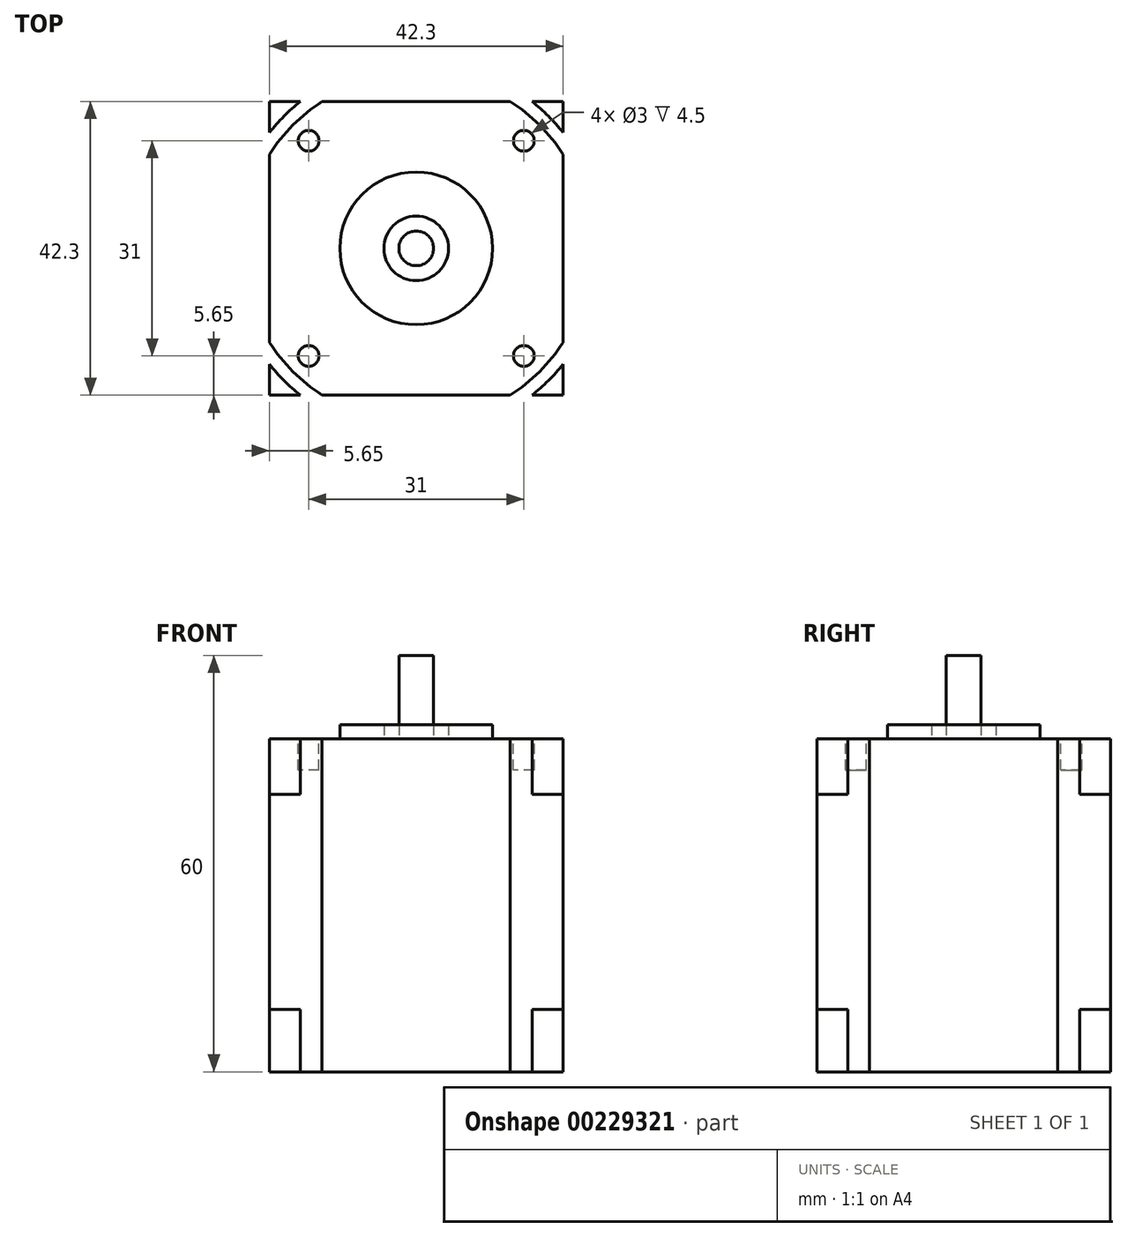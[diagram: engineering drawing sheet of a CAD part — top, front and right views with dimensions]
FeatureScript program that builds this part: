
annotation { "Feature Type Name" : "Feature", "Feature Type Description" : "" }
export const myFeature = defineFeature(function(context is Context, id is Id, definition is map)
    precondition{}
    {
        {
            var Q0;
            Q0=qCreatedBy(makeId("Top.planeOp"),FACE);
            var sketch = newSketch(context, id + "F0", { "sketchPlane" : qUnion([Q0])});
            skLineSegment(sketch, "E0.bottom", {"start": v(21.15, -21.15) * mm, "end": v(-21.15, -21.15) * mm});
            skLineSegment(sketch, "E0.top", {"start": v(21.15, 21.15) * mm, "end": v(-21.15, 21.15) * mm});
            skLineSegment(sketch, "E0.left", {"start": v(21.15, -21.15) * mm, "end": v(21.15, 21.15) * mm});
            skLineSegment(sketch, "E0.right", {"start": v(-21.15, -21.15) * mm, "end": v(-21.15, 21.15) * mm});
            skPoint(sketch, "E0.middle", {"position": v(0, 0) * mm});
            skCircle(sketch, "E1", {"center": v(0, 0) * mm, "radius": 26.94 * mm});
            skCircle(sketch, "E2", {"center": v(0, 0) * mm, "radius": 25.12 * mm});
            skCircle(sketch, "E3", {"center": v(0, 0) * mm, "radius": 4.65 * mm});
            skCircle(sketch, "E4", {"center": v(0, 0) * mm, "radius": 11 * mm});
            skCircle(sketch, "E5", {"center": v(0, 0) * mm, "radius": 2.5 * mm});
            skCircle(sketch, "E6", {"center": v(-15.5, 15.5) * mm, "radius": 1.5 * mm});
            skCircle(sketch, "E7.1.0", {"center": v(-15.5, -15.5) * mm, "radius": 1.5 * mm});
            skCircle(sketch, "E7.2.0", {"center": v(15.5, -15.5) * mm, "radius": 1.5 * mm});
            skCircle(sketch, "E7.3.0", {"center": v(15.5, 15.5) * mm, "radius": 1.5 * mm});
            skSolve(sketch);
        }
        {
            var Q0;
            Q0=makeQuery(id+"F0.imprint","IMPRINT",FACE,{"disambiguationData":[TD([[makeQuery(id+"F0.imprint","IMPRINT",EDGE,{"derivedFrom":sQuery(id+"F0.wireOp",EDGE,"E4")}),-1.0]])]});
            var Q1;
            Q1=makeQuery(id+"F0.imprint","IMPRINT",FACE,{"disambiguationData":[TD([[makeQuery(id+"F0.imprint","IMPRINT",EDGE,{"derivedFrom":sQuery(id+"F0.wireOp",EDGE,"E3")}),-1.0]])]});
            var Q2;
            Q2=makeQuery(id+"F0.imprint","IMPRINT",FACE,{"disambiguationData":[TD([[makeQuery(id+"F0.imprint","IMPRINT",EDGE,{"derivedFrom":sQuery(id+"F0.wireOp",EDGE,"E6")}),1.0]])]});
            var Q3;
            Q3=makeQuery(id+"F0.imprint","IMPRINT",FACE,{"disambiguationData":[TD([[makeQuery(id+"F0.imprint","IMPRINT",EDGE,{"derivedFrom":sQuery(id+"F0.wireOp",EDGE,"E7.3.0")}),1.0]])]});
            var Q4;
            Q4=makeQuery(id+"F0.imprint","IMPRINT",FACE,{"disambiguationData":[TD([[makeQuery(id+"F0.imprint","IMPRINT",EDGE,{"derivedFrom":sQuery(id+"F0.wireOp",EDGE,"E7.2.0")}),1.0]])]});
            var Q5;
            Q5=makeQuery(id+"F0.imprint","IMPRINT",FACE,{"disambiguationData":[TD([[makeQuery(id+"F0.imprint","IMPRINT",EDGE,{"derivedFrom":sQuery(id+"F0.wireOp",EDGE,"E7.1.0")}),1.0]])]});
            var Q6;
            Q6=makeQuery(id+"F0.imprint","IMPRINT",FACE,{"disambiguationData":[TD([[makeQuery(id+"F0.imprint","IMPRINT",EDGE,{"derivedFrom":sQuery(id+"F0.wireOp",EDGE,"E3")}),1.0]])]});
            var Q7;
            Q7=makeQuery(id+"F0.imprint","IMPRINT",FACE,{"disambiguationData":[TD([[makeQuery(id+"F0.imprint","IMPRINT",EDGE,{"derivedFrom":sQuery(id+"F0.wireOp",EDGE,"E5")}),1.0]])]});
            var Q8;
            {var subQ0=sQuery(id+"F0.wireOp",EDGE,"E1");var subQ1=sQuery(id+"F0.wireOp",EDGE,"E0.top");var subQ2=makeQuery(id+"F0.imprint","INTERSECT",VERTEX,{"disambiguationData":[OD(0.0)],"derivedFrom":[subQ1,subQ0]});Q8=makeQuery(id+"F0.imprint","IMPRINT",FACE,{"disambiguationData":[TD([[makeQuery(id+"F0.imprint","IMPRINT",EDGE,{"disambiguationData":[TD([[subQ2,-1.0]])],"derivedFrom":subQ1}),1.0]])]});}
            var Q9;
            {var subQ0=sQuery(id+"F0.wireOp",EDGE,"E1");var subQ1=sQuery(id+"F0.wireOp",EDGE,"E0.top");var subQ2=makeQuery(id+"F0.imprint","INTERSECT",VERTEX,{"disambiguationData":[OD(1.0)],"derivedFrom":[subQ1,subQ0]});Q9=makeQuery(id+"F0.imprint","IMPRINT",FACE,{"disambiguationData":[TD([[makeQuery(id+"F0.imprint","IMPRINT",EDGE,{"disambiguationData":[TD([[subQ2,1.0]])],"derivedFrom":subQ1}),1.0]])]});}
            var Q10;
            {var subQ0=sQuery(id+"F0.wireOp",EDGE,"E1");var subQ1=sQuery(id+"F0.wireOp",EDGE,"E0.bottom");var subQ2=makeQuery(id+"F0.imprint","INTERSECT",VERTEX,{"disambiguationData":[OD(1.0)],"derivedFrom":[subQ1,subQ0]});Q10=makeQuery(id+"F0.imprint","IMPRINT",FACE,{"disambiguationData":[TD([[makeQuery(id+"F0.imprint","IMPRINT",EDGE,{"disambiguationData":[TD([[subQ2,1.0]])],"derivedFrom":subQ1}),-1.0]])]});}
            var Q11;
            {var subQ0=sQuery(id+"F0.wireOp",EDGE,"E1");var subQ1=sQuery(id+"F0.wireOp",EDGE,"E0.bottom");var subQ2=makeQuery(id+"F0.imprint","INTERSECT",VERTEX,{"disambiguationData":[OD(0.0)],"derivedFrom":[subQ1,subQ0]});Q11=makeQuery(id+"F0.imprint","IMPRINT",FACE,{"disambiguationData":[TD([[makeQuery(id+"F0.imprint","IMPRINT",EDGE,{"disambiguationData":[TD([[subQ2,-1.0]])],"derivedFrom":subQ1}),-1.0]])]});}
            extrude(context, id + "F1", {"entities" : qUnion([Q0, Q1, Q2, Q3, Q4, Q5, Q6, Q7, Q8, Q9, Q10, Q11]), "oppositeDirection" : true, "depth" : 48 * mm});
        }
        {
            var Q0;
            {var subQ0=sQuery(id+"F0.wireOp",EDGE,"E1");var subQ1=sQuery(id+"F0.wireOp",EDGE,"E0.top");var subQ2=makeQuery(id+"F0.imprint","INTERSECT",VERTEX,{"disambiguationData":[OD(1.0)],"derivedFrom":[subQ1,subQ0]});Q0=makeQuery(id+"F0.imprint","IMPRINT",FACE,{"disambiguationData":[TD([[makeQuery(id+"F0.imprint","IMPRINT",EDGE,{"disambiguationData":[TD([[subQ2,1.0]])],"derivedFrom":subQ1}),1.0]])]});}
            var Q1;
            {var subQ0=sQuery(id+"F0.wireOp",EDGE,"E1");var subQ1=sQuery(id+"F0.wireOp",EDGE,"E0.bottom");var subQ2=makeQuery(id+"F0.imprint","INTERSECT",VERTEX,{"disambiguationData":[OD(1.0)],"derivedFrom":[subQ1,subQ0]});Q1=makeQuery(id+"F0.imprint","IMPRINT",FACE,{"disambiguationData":[TD([[makeQuery(id+"F0.imprint","IMPRINT",EDGE,{"disambiguationData":[TD([[subQ2,1.0]])],"derivedFrom":subQ1}),-1.0]])]});}
            var Q2;
            {var subQ0=sQuery(id+"F0.wireOp",EDGE,"E1");var subQ1=sQuery(id+"F0.wireOp",EDGE,"E0.top");var subQ2=makeQuery(id+"F0.imprint","INTERSECT",VERTEX,{"disambiguationData":[OD(0.0)],"derivedFrom":[subQ1,subQ0]});Q2=makeQuery(id+"F0.imprint","IMPRINT",FACE,{"disambiguationData":[TD([[makeQuery(id+"F0.imprint","IMPRINT",EDGE,{"disambiguationData":[TD([[subQ2,-1.0]])],"derivedFrom":subQ1}),1.0]])]});}
            var Q3;
            {var subQ0=sQuery(id+"F0.wireOp",EDGE,"E1");var subQ1=sQuery(id+"F0.wireOp",EDGE,"E0.bottom");var subQ2=makeQuery(id+"F0.imprint","INTERSECT",VERTEX,{"disambiguationData":[OD(0.0)],"derivedFrom":[subQ1,subQ0]});Q3=makeQuery(id+"F0.imprint","IMPRINT",FACE,{"disambiguationData":[TD([[makeQuery(id+"F0.imprint","IMPRINT",EDGE,{"disambiguationData":[TD([[subQ2,-1.0]])],"derivedFrom":subQ1}),-1.0]])]});}
            extrude(context, id + "F2", {"entities" : qUnion([Q0, Q1, Q2, Q3]), "operationType" : NewBodyOperationType.REMOVE, "oppositeDirection" : true, "depth" : 39 * mm, "hasSecondDirection" : true, "secondDirectionOppositeDirection" : true, "secondDirectionDepth" : 8 * mm});
        }
        {
            var Q0;
            Q0=makeQuery(id+"F0.imprint","IMPRINT",FACE,{"disambiguationData":[TD([[makeQuery(id+"F0.imprint","IMPRINT",EDGE,{"derivedFrom":sQuery(id+"F0.wireOp",EDGE,"E3")}),-1.0]])]});
            extrude(context, id + "F3", {"entities" : qUnion([Q0]), "operationType" : NewBodyOperationType.ADD, "depth" : 2 * mm});
        }
        {
            var Q0;
            Q0=makeQuery(id+"F0.imprint","IMPRINT",FACE,{"disambiguationData":[TD([[makeQuery(id+"F0.imprint","IMPRINT",EDGE,{"derivedFrom":sQuery(id+"F0.wireOp",EDGE,"E5")}),1.0]])]});
            extrude(context, id + "F4", {"entities" : qUnion([Q0]), "operationType" : NewBodyOperationType.ADD, "depth" : 12 * mm});
        }
        {
            var Q0;
            Q0=makeQuery(id+"F0.imprint","IMPRINT",FACE,{"disambiguationData":[TD([[makeQuery(id+"F0.imprint","IMPRINT",EDGE,{"derivedFrom":sQuery(id+"F0.wireOp",EDGE,"E6")}),1.0]])]});
            var Q1;
            Q1=makeQuery(id+"F0.imprint","IMPRINT",FACE,{"disambiguationData":[TD([[makeQuery(id+"F0.imprint","IMPRINT",EDGE,{"derivedFrom":sQuery(id+"F0.wireOp",EDGE,"E7.3.0")}),1.0]])]});
            var Q2;
            Q2=makeQuery(id+"F0.imprint","IMPRINT",FACE,{"disambiguationData":[TD([[makeQuery(id+"F0.imprint","IMPRINT",EDGE,{"derivedFrom":sQuery(id+"F0.wireOp",EDGE,"E7.2.0")}),1.0]])]});
            var Q3;
            Q3=makeQuery(id+"F0.imprint","IMPRINT",FACE,{"disambiguationData":[TD([[makeQuery(id+"F0.imprint","IMPRINT",EDGE,{"derivedFrom":sQuery(id+"F0.wireOp",EDGE,"E7.1.0")}),1.0]])]});
            extrude(context, id + "F5", {"entities" : qUnion([Q0, Q1, Q2, Q3]), "operationType" : NewBodyOperationType.REMOVE, "oppositeDirection" : true, "depth" : 4.5 * mm});
        }
    });
